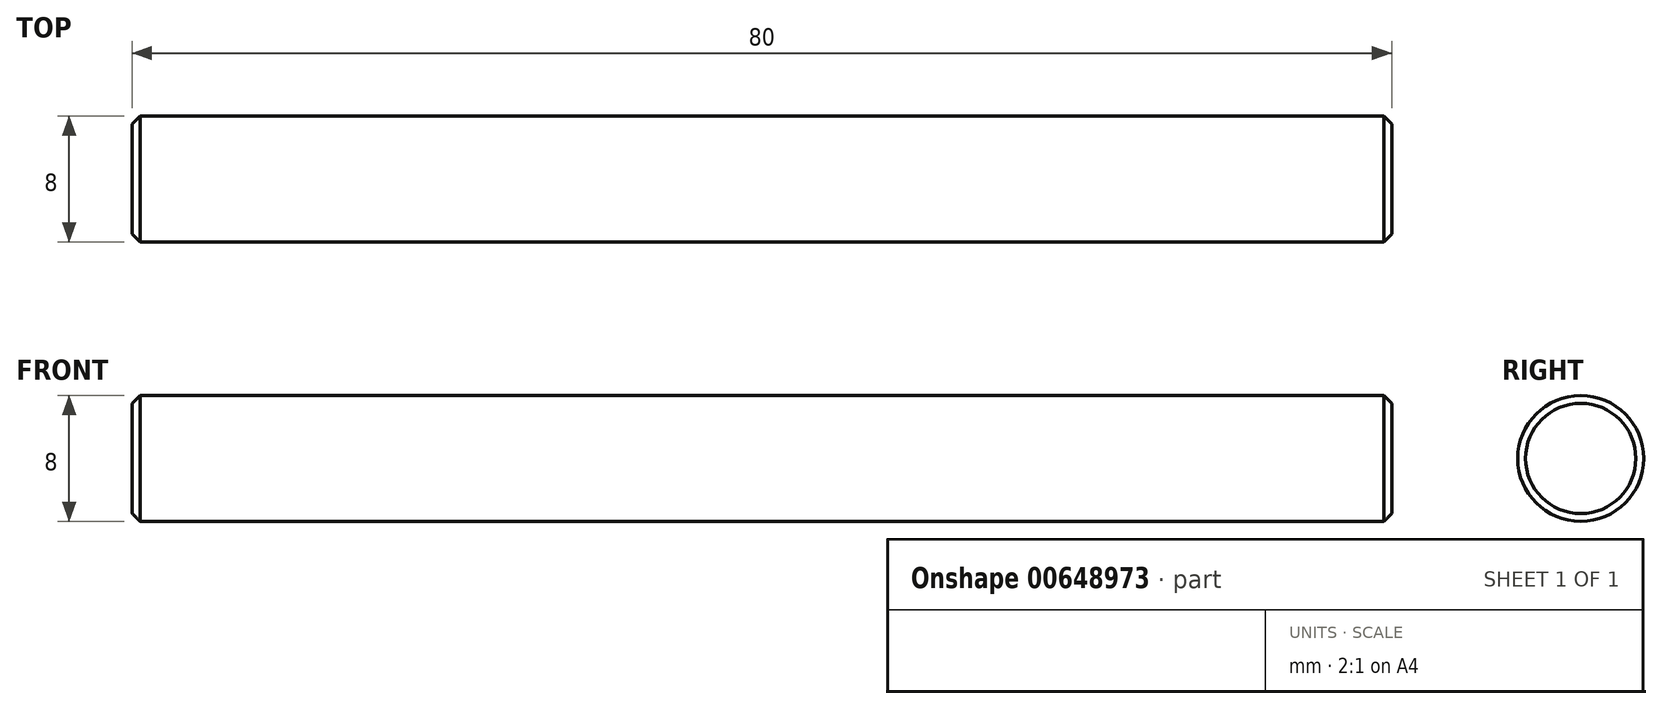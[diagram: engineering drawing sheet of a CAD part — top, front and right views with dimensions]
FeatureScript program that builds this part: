
annotation { "Feature Type Name" : "Feature", "Feature Type Description" : "" }
export const myFeature = defineFeature(function(context is Context, id is Id, definition is map)
    precondition{}
    {
        {
            var Q0;
            Q0=qCreatedBy(makeId("Right.planeOp"),FACE);
            var sketch = newSketch(context, id + "F0", { "sketchPlane" : qUnion([Q0])});
            skCircle(sketch, "E0", {"center": v(0, 0) * mm, "radius": 4 * mm});
            skSolve(sketch);
        }
        {
            var Q0;
            Q0 = qSketchRegion(id + "F0", true);
            extrude(context, id + "F1", {"entities" : qUnion([Q0]), "depth" : 80 * mm, "offsetDistance" : 25 * mm});
        }
        {
            var Q0;
            Q0=makeQuery(id+"F1.opExtrude","SWEPT_FACE",FACE,{"disambiguationData":[OSD([sQuery(id+"F0.wireOp",EDGE,"E0")])]});
            chamfer(context, id + "F2", {"entities" : qUnion([Q0]), "width" : 0.5 * mm, "tangentPropagation" : true});
        }
    });
